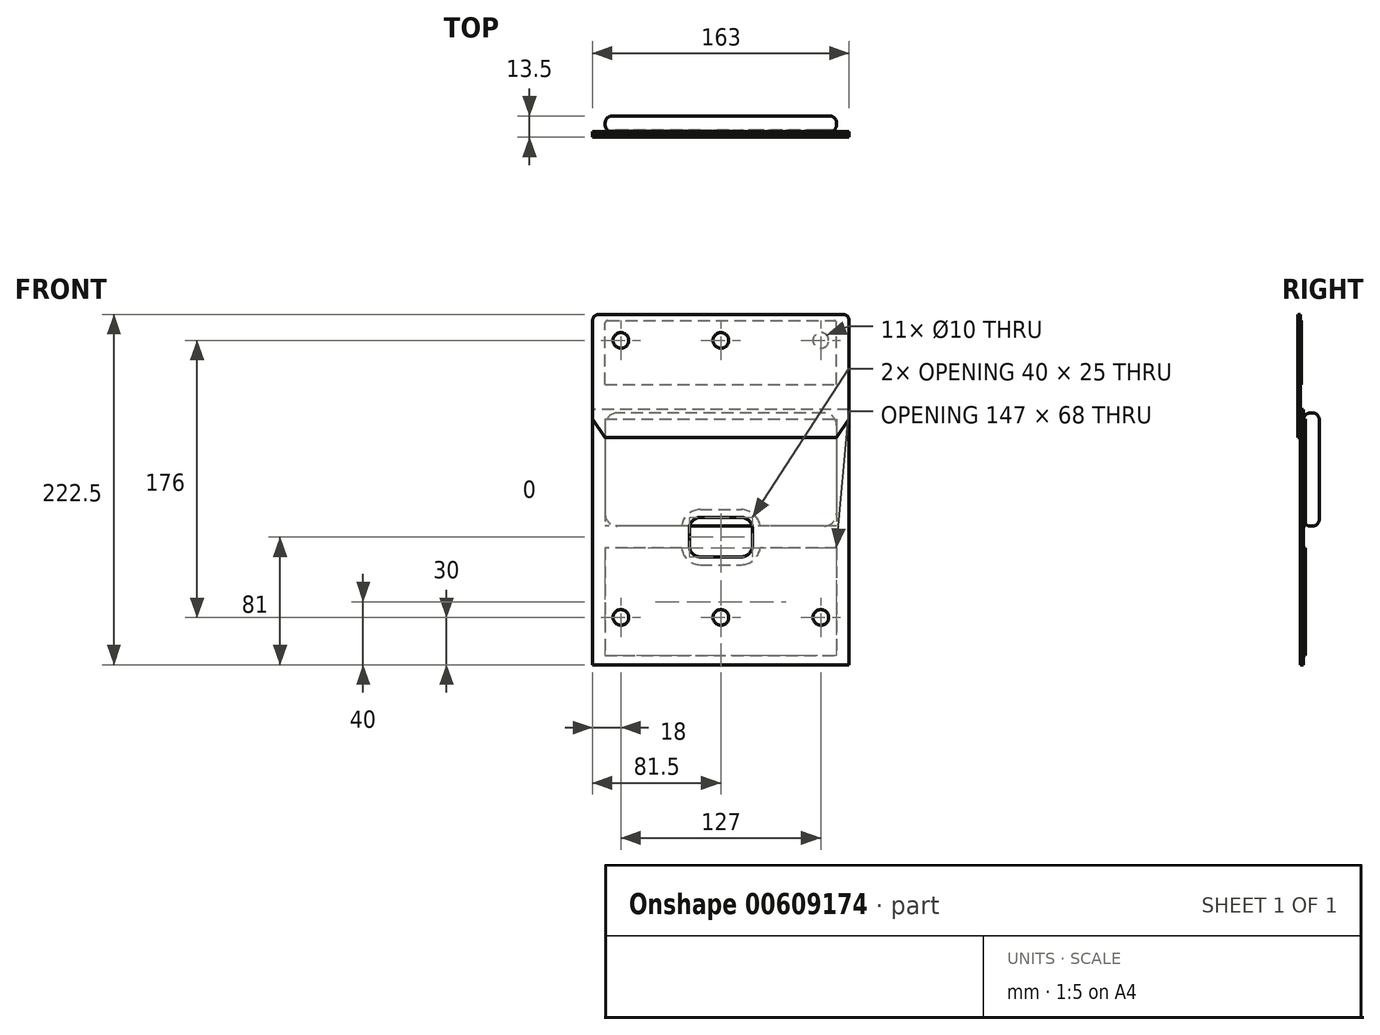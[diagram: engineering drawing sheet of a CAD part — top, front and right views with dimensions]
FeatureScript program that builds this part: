
annotation { "Feature Type Name" : "Feature", "Feature Type Description" : "" }
export const myFeature = defineFeature(function(context is Context, id is Id, definition is map)
    precondition{}
    {
        {
            var Q0;
            Q0=qCreatedBy(makeId("Front.planeOp"),FACE);
            var sketch = newSketch(context, id + "F0", { "sketchPlane" : qUnion([Q0])});
            skLineSegment(sketch, "E0.bottom", {"start": v(65.5, 36) * mm, "end": v(-65.5, 36) * mm});
            skLineSegment(sketch, "E0.top", {"start": v(65.5, -36) * mm, "end": v(-65.5, -36) * mm});
            skLineSegment(sketch, "E0.left", {"start": v(73.5, 28) * mm, "end": v(73.5, -28) * mm});
            skLineSegment(sketch, "E0.right", {"start": v(-73.5, 28) * mm, "end": v(-73.5, -28) * mm});
            skPoint(sketch, "E0.middle", {"position": v(0, 0) * mm});
            skPoint(sketch, "E1.visualSharp", {"position": v(-73.5, 36) * mm});
            skArc(sketch, "E1.filletArc", {"start": v(-65.5, 36) * mm, "mid": v(-71.16, 33.66) * mm, "end": v(-73.5, 28) * mm});
            skPoint(sketch, "E2.visualSharp", {"position": v(-73.5, -36) * mm});
            skArc(sketch, "E2.filletArc", {"start": v(-73.5, -28) * mm, "mid": v(-71.16, -33.66) * mm, "end": v(-65.5, -36) * mm});
            skPoint(sketch, "E3.visualSharp", {"position": v(73.5, -36) * mm});
            skArc(sketch, "E3.filletArc", {"start": v(65.5, -36) * mm, "mid": v(71.16, -33.66) * mm, "end": v(73.5, -28) * mm});
            skPoint(sketch, "E4.visualSharp", {"position": v(73.5, 36) * mm});
            skArc(sketch, "E4.filletArc", {"start": v(73.5, 28) * mm, "mid": v(71.16, 33.66) * mm, "end": v(65.5, 36) * mm});
            skSolve(sketch);
        }
        {
            var Q0;
            Q0=makeQuery(id+"F0.imprint","IMPRINT",FACE,{"disambiguationData":[TD([[makeQuery(id+"F0.imprint","IMPRINT",EDGE,{"derivedFrom":sQuery(id+"F0.wireOp",EDGE,"E0.bottom")}),1.0]])]});
            extrude(context, id + "F1", {"entities" : qUnion([Q0]), "endBound" : BoundingType.SYMMETRIC, "depth" : 10 * mm, "offsetDistance" : 25 * mm});
        }
        {
            var Q0;
            Q0=makeQuery(id+"F1.opExtrude","CAP_FACE",FACE,{"disambiguationData":[OSD([sQuery(id+"F0.wireOp",EDGE,"E0.bottom"),sQuery(id+"F0.wireOp",EDGE,"E0.top"),sQuery(id+"F0.wireOp",EDGE,"E0.left"),sQuery(id+"F0.wireOp",EDGE,"E0.right"),sQuery(id+"F0.wireOp",EDGE,"E1.filletArc"),sQuery(id+"F0.wireOp",EDGE,"E2.filletArc"),sQuery(id+"F0.wireOp",EDGE,"E3.filletArc"),sQuery(id+"F0.wireOp",EDGE,"E4.filletArc")])],"isStart":false});
            var Q1;
            Q1=makeQuery(id+"F1.opExtrude","CAP_FACE",FACE,{"disambiguationData":[OSD([sQuery(id+"F0.wireOp",EDGE,"E0.bottom"),sQuery(id+"F0.wireOp",EDGE,"E0.top"),sQuery(id+"F0.wireOp",EDGE,"E0.left"),sQuery(id+"F0.wireOp",EDGE,"E0.right"),sQuery(id+"F0.wireOp",EDGE,"E1.filletArc"),sQuery(id+"F0.wireOp",EDGE,"E2.filletArc"),sQuery(id+"F0.wireOp",EDGE,"E3.filletArc"),sQuery(id+"F0.wireOp",EDGE,"E4.filletArc")])],"isStart":true});
            fillet(context, id + "F2", {"entities" : qUnion([Q0, Q1]), "radius" : 4.5 * mm, "tangentPropagation" : true, "allowEdgeOverflow" : false});
        }
        {
            var Q0;
            Q0=makeQuery(id+"F1.opExtrude","CAP_FACE",FACE,{"disambiguationData":[OSD([sQuery(id+"F0.wireOp",EDGE,"E0.bottom"),sQuery(id+"F0.wireOp",EDGE,"E0.top"),sQuery(id+"F0.wireOp",EDGE,"E0.left"),sQuery(id+"F0.wireOp",EDGE,"E0.right"),sQuery(id+"F0.wireOp",EDGE,"E1.filletArc"),sQuery(id+"F0.wireOp",EDGE,"E2.filletArc"),sQuery(id+"F0.wireOp",EDGE,"E3.filletArc"),sQuery(id+"F0.wireOp",EDGE,"E4.filletArc")])],"isStart":false});
            var sketch = newSketch(context, id + "F3", { "sketchPlane" : qUnion([Q0])});
            skLineSegment(sketch, "E5.0", {"start": v(-65.5, 36) * mm, "end": v(65.5, 36) * mm});
            skLineSegment(sketch, "E6.0", {"start": v(-73.5, -122) * mm, "end": v(-73.5, 36) * mm, "construction": true});
            skLineSegment(sketch, "E7.0", {"start": v(73.5, 36) * mm, "end": v(73.5, -122) * mm, "construction": true});
            skLineSegment(sketch, "E8.0", {"start": v(73.5, -36) * mm, "end": v(24.9, -36) * mm});
            skPoint(sketch, "E9.orphan", {"position": v(-73.5, 28) * mm});
            skPoint(sketch, "E10.orphan", {"position": v(-65.5, 36) * mm});
            skPoint(sketch, "E11.orphan", {"position": v(73.5, 28) * mm});
            skPoint(sketch, "E12.orphan", {"position": v(65.5, 36) * mm});
            skLineSegment(sketch, "E13", {"start": v(-20, -43) * mm, "end": v(20, -43) * mm, "construction": true});
            skLineSegment(sketch, "E14.MirrorCS", {"start": v(-81.5, -122) * mm, "end": v(81.5, -122) * mm, "construction": true});
            skPoint(sketch, "E15.orphan", {"position": v(-73.5, -28) * mm});
            skPoint(sketch, "E16.orphan", {"position": v(73.5, -28) * mm});
            skLineSegment(sketch, "E17", {"start": v(-73.5, 32) * mm, "end": v(73.5, 32) * mm});
            skLineSegment(sketch, "E18", {"start": v(-81.5, 38) * mm, "end": v(-81.5, -124) * mm});
            skLineSegment(sketch, "E19.MirrorCS", {"start": v(81.5, 38) * mm, "end": v(81.5, -124) * mm});
            skPoint(sketch, "E20.orphan", {"position": v(81.5, 36) * mm});
            skPoint(sketch, "E21.orphan", {"position": v(0, 32) * mm});
            skPoint(sketch, "E22.orphan", {"position": v(-65.5, -36) * mm});
            skPoint(sketch, "E23.orphan", {"position": v(65.5, -36) * mm});
            skLineSegment(sketch, "E24", {"start": v(-73.5, 32) * mm, "end": v(-73.5, -36) * mm});
            skLineSegment(sketch, "E25", {"start": v(73.5, 32) * mm, "end": v(73.5, -36) * mm});
            skLineSegment(sketch, "E26.trimOffspring", {"start": v(-24.9, -36) * mm, "end": v(-73.5, -36) * mm});
            skLineSegment(sketch, "E27.MirrorCS", {"start": v(-24.9, -50) * mm, "end": v(-73.5, -50) * mm});
            skLineSegment(sketch, "E28.MirrorCS", {"start": v(-73.5, 36) * mm, "end": v(-73.5, -122) * mm, "construction": true});
            skLineSegment(sketch, "E29.MirrorCS", {"start": v(-73.5, -118) * mm, "end": v(73.5, -118) * mm});
            skLineSegment(sketch, "E30.MirrorCS", {"start": v(73.5, -50) * mm, "end": v(24.9, -50) * mm});
            skLineSegment(sketch, "E31", {"start": v(-73.5, -50) * mm, "end": v(-73.5, -118) * mm});
            skLineSegment(sketch, "E32", {"start": v(73.5, -50) * mm, "end": v(73.5, -118) * mm});
            skCircle(sketch, "E33", {"center": v(63.5, -94) * mm, "radius": 5 * mm});
            skCircle(sketch, "E34.MirrorC", {"center": v(-63.5, -94) * mm, "radius": 5 * mm});
            skLineSegment(sketch, "E35", {"start": v(81.5, 38) * mm, "end": v(-81.5, 38) * mm});
            skPoint(sketch, "E36.orphan", {"position": v(-81.5, 36) * mm});
            skLineSegment(sketch, "E37.MirrorCS", {"start": v(81.5, -124) * mm, "end": v(-81.5, -124) * mm});
            skLineSegment(sketch, "E38.bottom", {"start": v(-13, -30.5) * mm, "end": v(13, -30.5) * mm});
            skLineSegment(sketch, "E38.top", {"start": v(-13, -55.5) * mm, "end": v(13, -55.5) * mm});
            skLineSegment(sketch, "E38.left", {"start": v(-20, -37.5) * mm, "end": v(-20, -48.5) * mm});
            skLineSegment(sketch, "E38.right", {"start": v(20, -37.5) * mm, "end": v(20, -48.5) * mm});
            skPoint(sketch, "E39.visualSharp", {"position": v(-20, -30.5) * mm});
            skArc(sketch, "E39.filletArc", {"start": v(-13, -30.5) * mm, "mid": v(-17.95, -32.55) * mm, "end": v(-20, -37.5) * mm});
            skPoint(sketch, "E40.visualSharp", {"position": v(-20, -55.5) * mm});
            skArc(sketch, "E40.filletArc", {"start": v(-20, -48.5) * mm, "mid": v(-17.95, -53.45) * mm, "end": v(-13, -55.5) * mm});
            skPoint(sketch, "E41.visualSharp", {"position": v(20, -55.5) * mm});
            skArc(sketch, "E41.filletArc", {"start": v(13, -55.5) * mm, "mid": v(17.95, -53.45) * mm, "end": v(20, -48.5) * mm});
            skPoint(sketch, "E42.visualSharp", {"position": v(20, -30.5) * mm});
            skArc(sketch, "E42.filletArc", {"start": v(20, -37.5) * mm, "mid": v(17.95, -32.55) * mm, "end": v(13, -30.5) * mm});
            skArc(sketch, "E43", {"start": v(-13, -25.5) * mm, "mid": v(-20.94, -28.5) * mm, "end": v(-24.9, -36) * mm});
            skLineSegment(sketch, "E44", {"start": v(-13, -25.5) * mm, "end": v(13, -25.5) * mm});
            skPoint(sketch, "E45.orphan", {"position": v(-22.7, -36) * mm});
            skPoint(sketch, "E46.orphan", {"position": v(22.7, -36) * mm});
            skArc(sketch, "E47.MirrorCS", {"start": v(13, -25.5) * mm, "mid": v(20.94, -28.5) * mm, "end": v(24.9, -36) * mm});
            skArc(sketch, "E48.MirrorCS", {"start": v(-13, -60.5) * mm, "mid": v(-20.94, -57.5) * mm, "end": v(-24.9, -50) * mm});
            skLineSegment(sketch, "E49.MirrorCS", {"start": v(-13, -60.5) * mm, "end": v(13, -60.5) * mm});
            skArc(sketch, "E50.MirrorCS", {"start": v(13, -60.5) * mm, "mid": v(20.94, -57.5) * mm, "end": v(24.9, -50) * mm});
            skPoint(sketch, "E51.orphan", {"position": v(-22.7, -50) * mm});
            skPoint(sketch, "E52.orphan", {"position": v(22.7, -50) * mm});
            skCircle(sketch, "E53", {"center": v(0, -94) * mm, "radius": 5 * mm});
            skSolve(sketch);
        }
        {
            var Q0;
            Q0 = qSketchRegion(id + "F3", true);
            var Q1;
            {var subQ10=sQuery(id+"F3.wireOp",EDGE,"E44");Q1=makeQuery(id+"F3.imprint","IMPRINT",FACE,{"disambiguationData":[TD([[makeQuery(id+"F3.imprint","IMPRINT",EDGE,{"derivedFrom":subQ10}),1.0]])]});}
            var Q2;
            Q2=makeQuery(id+"F3.imprint","IMPRINT",FACE,{"disambiguationData":[TD([[makeQuery(id+"F3.imprint","IMPRINT",EDGE,{"derivedFrom":sQuery(id+"F3.wireOp",EDGE,"E27.MirrorCS")}),1.0]])]});
            var Q3;
            {var subQ10=sQuery(id+"F3.wireOp",EDGE,"E8.0");Q3=makeQuery(id+"F3.imprint","IMPRINT",FACE,{"disambiguationData":[TD([[makeQuery(id+"F3.imprint","IMPRINT",EDGE,{"derivedFrom":subQ10}),-1.0]])]});}
            extrude(context, id + "F4", {"entities" : qUnion([Q0, Q1, Q2, Q3]), "depth" : 2 * mm, "offsetDistance" : 25 * mm});
        }
        {
            var Q0;
            {var subQ10=sQuery(id+"F3.wireOp",EDGE,"E8.0");Q0=makeQuery(id+"F3.imprint","IMPRINT",FACE,{"disambiguationData":[TD([[makeQuery(id+"F3.imprint","IMPRINT",EDGE,{"derivedFrom":subQ10}),-1.0]])]});}
            var Q1;
            {var subQ10=sQuery(id+"F3.wireOp",EDGE,"E44");Q1=makeQuery(id+"F3.imprint","IMPRINT",FACE,{"disambiguationData":[TD([[makeQuery(id+"F3.imprint","IMPRINT",EDGE,{"derivedFrom":subQ10}),1.0]])]});}
            var Q2;
            Q2=makeQuery(id+"F3.imprint","IMPRINT",FACE,{"disambiguationData":[TD([[makeQuery(id+"F3.imprint","IMPRINT",EDGE,{"derivedFrom":sQuery(id+"F3.wireOp",EDGE,"E27.MirrorCS")}),1.0]])]});
            extrude(context, id + "F5", {"entities" : qUnion([Q0, Q1, Q2]), "oppositeDirection" : true, "depth" : 1 * mm, "offsetDistance" : 25 * mm});
        }
        {
            var Q0;
            Q0=makeQuery(id+"F4.opExtrude","CAP_FACE",FACE,{"disambiguationData":[OSD([sQuery(id+"F3.wireOp",EDGE,"E18"),sQuery(id+"F3.wireOp",EDGE,"E19.MirrorCS"),sQuery(id+"F3.wireOp",EDGE,"E33"),sQuery(id+"F3.wireOp",EDGE,"E34.MirrorC"),sQuery(id+"F3.wireOp",EDGE,"E35"),sQuery(id+"F3.wireOp",EDGE,"E37.MirrorCS"),sQuery(id+"F3.wireOp",EDGE,"E38.bottom"),sQuery(id+"F3.wireOp",EDGE,"E38.top"),sQuery(id+"F3.wireOp",EDGE,"E38.left"),sQuery(id+"F3.wireOp",EDGE,"E38.right"),sQuery(id+"F3.wireOp",EDGE,"E39.filletArc"),sQuery(id+"F3.wireOp",EDGE,"E40.filletArc"),sQuery(id+"F3.wireOp",EDGE,"E41.filletArc"),sQuery(id+"F3.wireOp",EDGE,"E42.filletArc")])],"isStart":false});
            var sketch = newSketch(context, id + "F6", { "sketchPlane" : qUnion([Q0])});
            skLineSegment(sketch, "E54", {"start": v(-81.5, 94.5) * mm, "end": v(-81.5, 32) * mm});
            skLineSegment(sketch, "E55", {"start": v(-81.5, 32) * mm, "end": v(-73.5, 20.16) * mm});
            skLineSegment(sketch, "E56", {"start": v(-73.5, 20.16) * mm, "end": v(0, 20.16) * mm});
            skLineSegment(sketch, "E57", {"start": v(0, 98.5) * mm, "end": v(-77.5, 98.5) * mm});
            skLineSegment(sketch, "E58", {"start": v(-88.59, 54) * mm, "end": v(5.64, 54) * mm, "construction": true});
            skPoint(sketch, "E59.visualSharp", {"position": v(-81.5, 98.5) * mm});
            skArc(sketch, "E59.filletArc", {"start": v(-77.5, 98.5) * mm, "mid": v(-80.33, 97.32) * mm, "end": v(-81.5, 94.5) * mm});
            skLineSegment(sketch, "E60.MirrorCS", {"start": v(0, 98.5) * mm, "end": v(77.5, 98.5) * mm});
            skArc(sketch, "E61.MirrorCS", {"start": v(77.5, 98.5) * mm, "mid": v(80.33, 97.32) * mm, "end": v(81.5, 94.5) * mm});
            skLineSegment(sketch, "E62.MirrorCS", {"start": v(81.5, 94.5) * mm, "end": v(81.5, 32) * mm});
            skLineSegment(sketch, "E63.MirrorCS", {"start": v(81.5, 32) * mm, "end": v(73.5, 20.16) * mm});
            skLineSegment(sketch, "E64.MirrorCS", {"start": v(73.5, 20.16) * mm, "end": v(0, 20.16) * mm});
            skLineSegment(sketch, "E65.bottom", {"start": v(-73.5, 54) * mm, "end": v(73.5, 54) * mm});
            skLineSegment(sketch, "E65.top", {"start": v(-72, 94.5) * mm, "end": v(72, 94.5) * mm});
            skLineSegment(sketch, "E65.left", {"start": v(-73.5, 54) * mm, "end": v(-73.5, 93) * mm});
            skLineSegment(sketch, "E65.right", {"start": v(73.5, 54) * mm, "end": v(73.5, 93) * mm});
            skArc(sketch, "E66.filletArc", {"start": v(-72, 94.5) * mm, "mid": v(-73.06, 94.06) * mm, "end": v(-73.5, 93) * mm});
            skArc(sketch, "E67.filletArc", {"start": v(73.5, 93) * mm, "mid": v(73.06, 94.06) * mm, "end": v(72, 94.5) * mm});
            skCircle(sketch, "E68", {"center": v(63.5, 82) * mm, "radius": 5 * mm});
            skCircle(sketch, "E69.MirrorC", {"center": v(-63.5, 82) * mm, "radius": 5 * mm});
            skCircle(sketch, "E70", {"center": v(0, 82) * mm, "radius": 5 * mm});
            skSolve(sketch);
        }
        {
            var Q0;
            Q0=makeQuery(id+"F6.imprint","IMPRINT",FACE,{"disambiguationData":[TD([[makeQuery(id+"F6.imprint","IMPRINT",EDGE,{"derivedFrom":sQuery(id+"F6.wireOp",EDGE,"E57")}),1.0]])]});
            var Q1;
            {var subQ3=sQuery(id+"F6.wireOp",EDGE,"E55");Q1=makeQuery(id+"F6.imprint","IMPRINT",FACE,{"disambiguationData":[TD([[makeQuery(id+"F6.imprint","IMPRINT",EDGE,{"derivedFrom":subQ3}),1.0]])]});}
            var Q2;
            Q2=makeQuery(id+"F6.imprint","IMPRINT",FACE,{"disambiguationData":[TD([[makeQuery(id+"F6.imprint","IMPRINT",EDGE,{"derivedFrom":sQuery(id+"F6.wireOp",EDGE,"E65.bottom")}),1.0]])]});
            var Q3;
            Q3=makeQuery(id+"F6.imprint","IMPRINT",FACE,{"disambiguationData":[TD([[makeQuery(id+"F6.imprint","IMPRINT",EDGE,{"derivedFrom":sQuery(id+"F6.wireOp",EDGE,"E68")}),1.0]])]});
            var Q4;
            Q4=makeQuery(id+"F6.imprint","IMPRINT",FACE,{"disambiguationData":[TD([[makeQuery(id+"F6.imprint","IMPRINT",EDGE,{"derivedFrom":sQuery(id+"F6.wireOp",EDGE,"E69.MirrorC")}),-1.0]])]});
            extrude(context, id + "F7", {"entities" : qUnion([Q0, Q1, Q2, Q3, Q4]), "depth" : 1.5 * mm, "offsetDistance" : 25 * mm});
        }
        {
            var Q0;
            Q0=makeQuery(id+"F6.imprint","IMPRINT",FACE,{"disambiguationData":[TD([[makeQuery(id+"F6.imprint","IMPRINT",EDGE,{"derivedFrom":sQuery(id+"F6.wireOp",EDGE,"E65.bottom")}),1.0]])]});
            extrude(context, id + "F8", {"entities" : qUnion([Q0]), "oppositeDirection" : true, "depth" : 0.55 * mm, "offsetDistance" : 25 * mm});
        }
        {
            var Q0;
            Q0 = qSketchRegion(id + "F3", true);
            var Q1;
            {var subQ10=sQuery(id+"F3.wireOp",EDGE,"E8.0");Q1=makeQuery(id+"F3.imprint","IMPRINT",FACE,{"disambiguationData":[TD([[makeQuery(id+"F3.imprint","IMPRINT",EDGE,{"derivedFrom":subQ10}),-1.0]])]});}
            var Q2;
            {var subQ10=sQuery(id+"F3.wireOp",EDGE,"E44");Q2=makeQuery(id+"F3.imprint","IMPRINT",FACE,{"disambiguationData":[TD([[makeQuery(id+"F3.imprint","IMPRINT",EDGE,{"derivedFrom":subQ10}),1.0]])]});}
            var Q3;
            Q3=makeQuery(id+"F28tSR27ECiH4KY_1.opExtrude","CAP_FACE",FACE,{"disambiguationData":[OSD([sQuery(id+"F3.wireOp",EDGE,"E27.MirrorCS"),sQuery(id+"F3.wireOp",EDGE,"E29.MirrorCS"),sQuery(id+"F3.wireOp",EDGE,"E30.MirrorCS"),sQuery(id+"F3.wireOp",EDGE,"E31"),sQuery(id+"F3.wireOp",EDGE,"E32"),sQuery(id+"F3.wireOp",EDGE,"E33"),sQuery(id+"F3.wireOp",EDGE,"E34.MirrorC"),sQuery(id+"F3.wireOp",EDGE,"E48.MirrorCS"),sQuery(id+"F3.wireOp",EDGE,"E49.MirrorCS"),sQuery(id+"F3.wireOp",EDGE,"E50.MirrorCS")])],"isStart":false});
            extrude(context, id + "F9", {"entities" : qUnion([Q0, Q1, Q2, Q3]), "depth" : 1 * mm, "offsetDistance" : 25 * mm});
        }
    });
